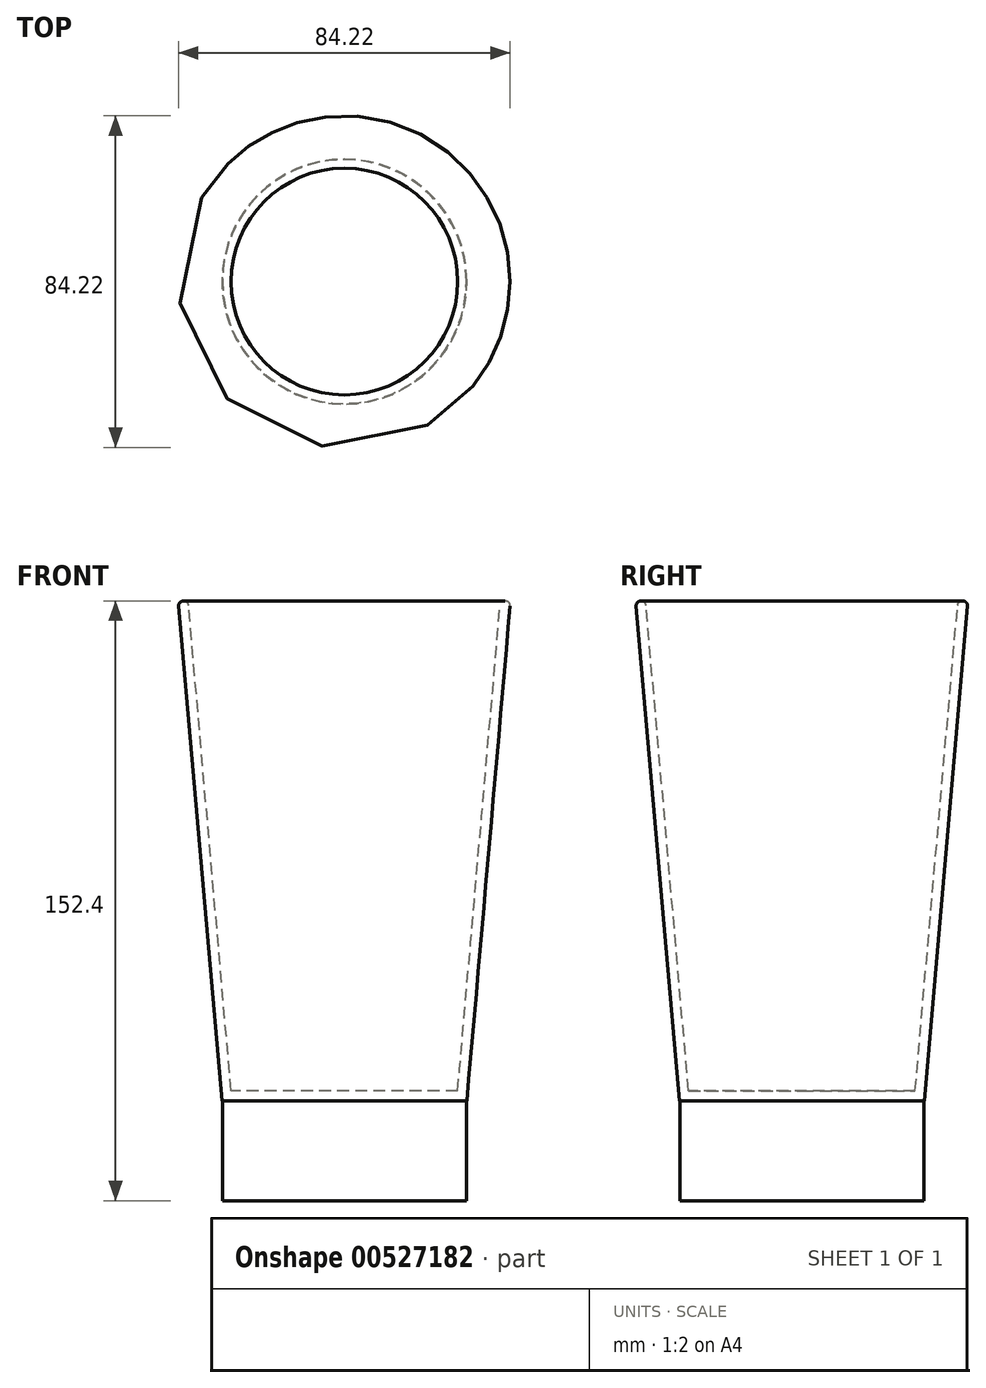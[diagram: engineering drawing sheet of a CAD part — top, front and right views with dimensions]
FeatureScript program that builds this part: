
annotation { "Feature Type Name" : "Feature", "Feature Type Description" : "" }
export const myFeature = defineFeature(function(context is Context, id is Id, definition is map)
    precondition{}
    {
        {
            var Q0;
            Q0=qCreatedBy(makeId("Top.planeOp"),FACE);
            var sketch = newSketch(context, id + "F0", { "sketchPlane" : qUnion([Q0])});
            skCircle(sketch, "E0", {"center": v(0, 0) * mm, "radius": 44.45 * mm});
            skSolve(sketch);
        }
        {
            var Q0;
            Q0 = qSketchRegion(id + "F0", true);
            extrude(context, id + "F1", {"entities" : qUnion([Q0]), "endBound" : BoundingType.SYMMETRIC, "depth" : 127 * mm, "offsetDistance" : 25.4 * mm});
        }
        {
            var Q0;
            Q0=makeQuery(id+"F1.opExtrude","CAP_EDGE",EDGE,{"disambiguationData":[OSD([sQuery(id+"F0.wireOp",EDGE,"E0")])],"isStart":true});
            chamfer(context, id + "F2", {"entities" : qUnion([Q0]), "chamferType" : ChamferType.OFFSET_ANGLE, "width" : 152.4 * mm, "oppositeDirection" : false, "angle" : 5 * degree, "tangentPropagation" : true});
        }
        {
            var Q0;
            Q0=makeQuery(id+"F1.opExtrude","CAP_FACE",FACE,{"disambiguationData":[OSD([sQuery(id+"F0.wireOp",EDGE,"E0")])],"isStart":false});
            shell(context, id + "F3", {"entities" : qUnion([Q0]), "thickness" : 2.54 * mm});
        }
        {
            var Q0;
            {var subQ0=sQuery(id+"F0.wireOp",EDGE,"E0");Q0=makeQuery(id+"F3.opShell","OFFSET_EDGE",EDGE,{"disambiguationData":[OSD([subQ0]),TDD([makeQuery(id+"F2.opChamfer","BLEND_EDGE",EDGE,{"blendedFrom":[makeQuery(id+"F1.opExtrude","CAP_EDGE",EDGE,{"disambiguationData":[OSD([subQ0])],"isStart":true}),makeQuery(id+"F1.opExtrude","CAP_FACE",FACE,{"disambiguationData":[OSD([subQ0])],"isStart":false})],"blendedInto":[makeQuery(id+"F1.opExtrude","CAP_FACE",FACE,{"disambiguationData":[OSD([subQ0])],"isStart":false})]})])]});}
            var Q1;
            {var subQ0=sQuery(id+"F0.wireOp",EDGE,"E0");Q1=makeQuery(id+"F2.opChamfer","BLEND_EDGE",EDGE,{"blendedFrom":[makeQuery(id+"F1.opExtrude","CAP_EDGE",EDGE,{"disambiguationData":[OSD([subQ0])],"isStart":true}),makeQuery(id+"F1.opExtrude","CAP_FACE",FACE,{"disambiguationData":[OSD([subQ0])],"isStart":false})],"blendedInto":[makeQuery(id+"F1.opExtrude","CAP_FACE",FACE,{"disambiguationData":[OSD([subQ0])],"isStart":false})]});}
            fillet(context, id + "F4", {"entities" : qUnion([Q0, Q1]), "radius" : 1.27 * mm, "tangentPropagation" : true, "allowEdgeOverflow" : false});
        }
        {
            var Q0;
            Q0=makeQuery(id+"F1.opExtrude","CAP_FACE",FACE,{"disambiguationData":[OSD([sQuery(id+"F0.wireOp",EDGE,"E0")])],"isStart":true});
            var sketch = newSketch(context, id + "F5", { "sketchPlane" : qUnion([Q0])});
            skCircle(sketch, "E1", {"center": v(0, 0) * mm, "radius": 30.99 * mm});
            skSolve(sketch);
        }
        {
            var Q0;
            Q0 = qSketchRegion(id + "F5", true);
            extrude(context, id + "F6", {"entities" : qUnion([Q0]), "operationType" : NewBodyOperationType.ADD, "depth" : 25.4 * mm, "offsetDistance" : 25.4 * mm});
        }
    });
